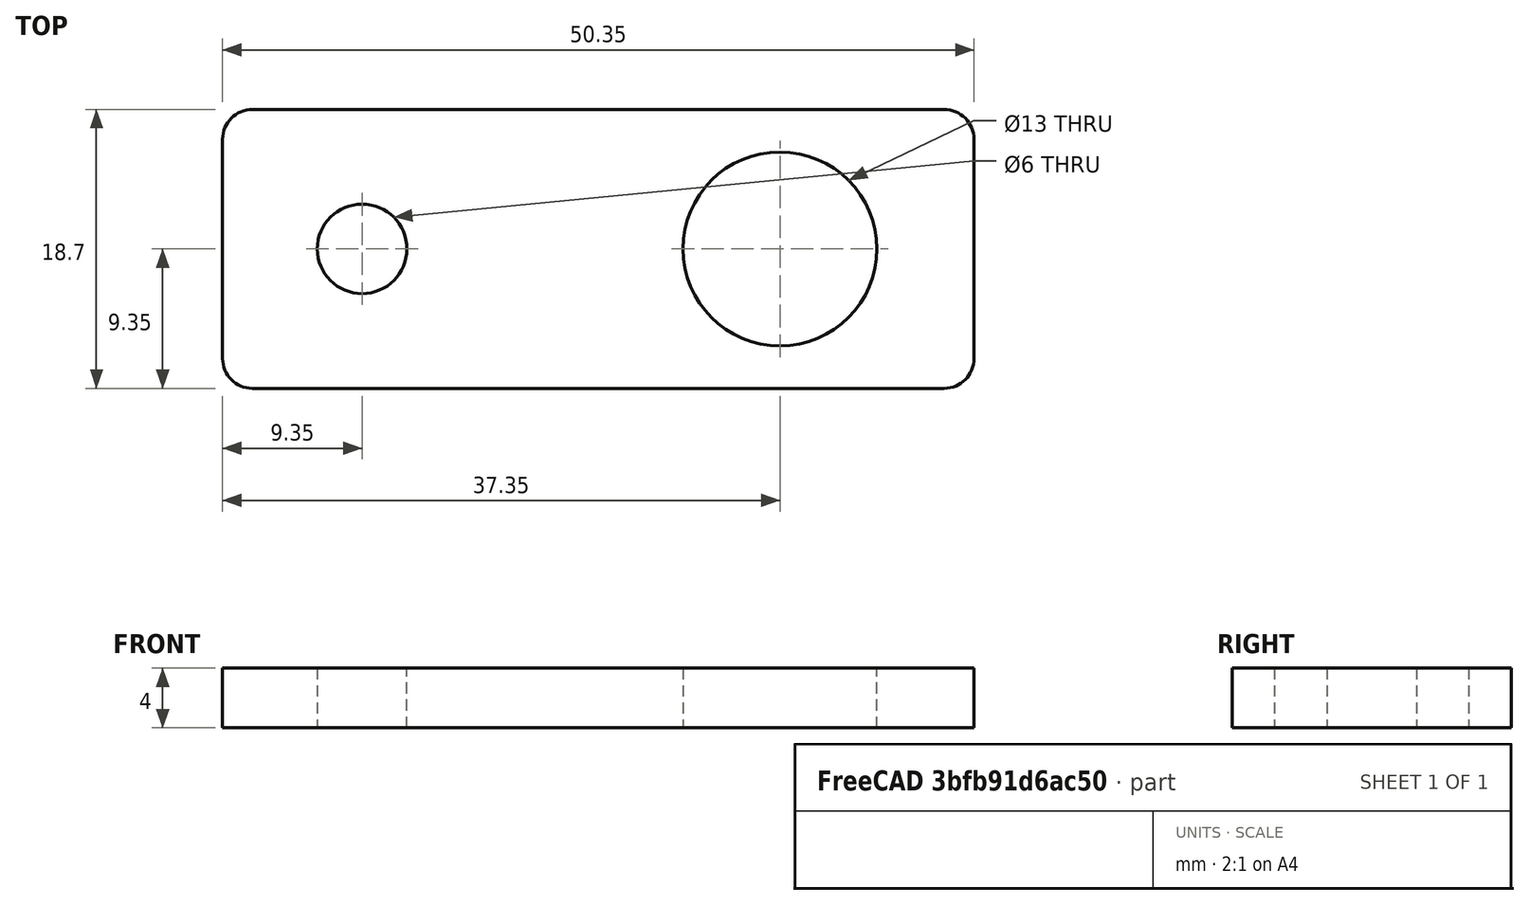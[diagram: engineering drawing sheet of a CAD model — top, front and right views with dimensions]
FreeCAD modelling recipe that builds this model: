
FCSTD DOCUMENT  (FreeCAD 0.19R24267 +99 (Git))
Label: V2 Flexible coolant pipe mount for LEDs
License: All rights reserved
LicenseURL: http://en.wikipedia.org/wiki/All_rights_reserved
objects: Sketcher::SketchObject×1, PartDesign::Pad×1, PartDesign::Body×1
note: 4 computed .brp shape members not serialized (recipe doc carries the construction recipe); baked Part::Feature solids carry a one-line shape summary decoded from their .brp

FEATURE [Sketcher::SketchObject] Sketch
  FullyConstrained = true
  MapMode = 5
  Support = -> [XY_Plane]
  sketch-geometry (21):
    g0: LineSegment StartX=2 StartY=9.35 StartZ=0 EndX=48.35 EndY=9.35 EndZ=0
    g1: LineSegment StartX=2 StartY=-9.35 StartZ=0 EndX=48.35 EndY=-9.35 EndZ=0
    g2: LineSegment StartX=0 StartY=7.35 StartZ=0 EndX=0 EndY=-7.35 EndZ=0
    g3: LineSegment StartX=50.35 StartY=7.35 StartZ=0 EndX=50.35 EndY=-7.35 EndZ=0
    g4: ArcOfCircle CenterX=2 CenterY=7.35 CenterZ=0 NormalX=0 NormalY=0 NormalZ=1 AngleXU=0 Radius=2 StartAngle=1.5708 EndAngle=3.14159
    g5: ArcOfCircle CenterX=2 CenterY=-7.35 CenterZ=0 NormalX=0 NormalY=0 NormalZ=1 AngleXU=0 Radius=2 StartAngle=3.14159 EndAngle=4.71239
    g6: ArcOfCircle CenterX=48.35 CenterY=7.35 CenterZ=0 NormalX=0 NormalY=0 NormalZ=1 AngleXU=0 Radius=2 StartAngle=0 EndAngle=1.5708
    g7: ArcOfCircle CenterX=48.35 CenterY=-7.35 CenterZ=0 NormalX=0 NormalY=0 NormalZ=1 AngleXU=0 Radius=2 StartAngle=4.71239 EndAngle=6.28319
    g8: Circle CenterX=9.35 CenterY=0 CenterZ=0 NormalX=0 NormalY=0 NormalZ=1 AngleXU=0 Radius=3
    g9: Circle CenterX=37.35 CenterY=0 CenterZ=0 NormalX=0 NormalY=0 NormalZ=1 AngleXU=0 Radius=6.5
    g10: LineSegment StartX=26.3803 StartY=0 StartZ=0 EndX=31.8652 EndY=-9.5 EndZ=0
    g11: LineSegment StartX=31.8652 StartY=-9.5 StartZ=0 EndX=42.8348 EndY=-9.5 EndZ=0
    g12: LineSegment StartX=42.8348 StartY=-9.5 StartZ=0 EndX=48.3197 EndY=-3.3005e-12 EndZ=0
    g13: LineSegment StartX=48.3197 StartY=-3.3005e-12 StartZ=0 EndX=42.8348 EndY=9.5 EndZ=0
    g14: LineSegment StartX=42.8348 StartY=9.5 StartZ=0 EndX=31.8652 EndY=9.5 EndZ=0
    g15: LineSegment StartX=31.8652 StartY=9.5 StartZ=0 EndX=26.3803 EndY=0 EndZ=0
    g16: Circle CenterX=37.35 CenterY=0 CenterZ=0 NormalX=0 NormalY=0 NormalZ=1 AngleXU=0 Radius=10.9697
    g17: LineSegment StartX=19.35 StartY=9.35 StartZ=0 EndX=19.35 EndY=-9.35 EndZ=0
    g18: GeomPoint X=19.35 Y=0 Z=0
    g19: GeomPoint X=50.35 Y=0 Z=0
    g20: Circle CenterX=9.35 CenterY=0 CenterZ=0 NormalX=0 NormalY=0 NormalZ=1 AngleXU=0 Radius=13
  constraints (51):
    c: Horizontal(g0)
    c: Horizontal(g1)
    c: Vertical(g3)
    c: Tangent(g2,g4) = -1.5708
    c: Tangent(g0,g4) = 1.5708
    c: Tangent(g2,g5) = -1.5708
    c: Tangent(g1,g5) = -1.5708
    c: Tangent(g0,g6) = 1.5708
    c: Tangent(g3,g6) = 1.5708
    c: Tangent(g3,g7) = 1.5708
    c: Tangent(g1,g7) = -1.5708
    c: Symmetric(g2,g2,g-1)
    c: PointOnObject(g-1,g2)
    c: Equal(g7,g5)
    c: Equal(g5,g4)
    c: Equal(g4,g6)
    c: Radius(g4) = 2
    c: DistanceY(g1,g0) = 18.7
    c: PointOnObject(g8,g-1)
    c: PointOnObject(g9,g-1)
    c: DistanceX(g-1,g8) = 9.35
    c: Radius(g8) = 3
    c: Coincident(g10,g11)
    c: Coincident(g11,g12)
    c: Coincident(g12,g13)
    c: Coincident(g13,g14)
    c: Coincident(g14,g15)
    c: Coincident(g15,g10)
    c: Equal(g10, g11-g15) x5
    c: PointOnObject(g10,g16)
    c: PointOnObject(g11,g16)
    c: PointOnObject(g12,g16)
    c: PointOnObject(g13,g16)
    c: PointOnObject(g14,g16)
    c: PointOnObject(g15,g16)
    c: Coincident(g16,g9)
    c: PointOnObject(g15,g-1)
    c: DistanceY(g11,g13) = 19
    c: PointOnObject(g17,g0)
    c: PointOnObject(g17,g1)
    c: Vertical(g17)
    c: DistanceX(g8,g17) = 10
    c: PointOnObject(g18,g-1)
    c: PointOnObject(g18,g17)
    c: PointOnObject(g19,g3)
    c: Coincident(g20,g8)
    c: Radius(g20) = 13
    c: DistanceX(g9,g19) = 13
    c: DistanceX(g18,g9) = 18
    c: PointOnObject(g19,g-1)
    c: Diameter(g9) = 13
FEATURE [PartDesign::Pad] Pad
  Direction = (1,1,1)
  Length = 4
  Length2 = 100
  Profile = -> Sketch
  Type = 0
FEATURE [PartDesign::Body] Body
  Group = -> [Sketch,Pad]
  Origin = -> Origin
  Tip = -> Pad
